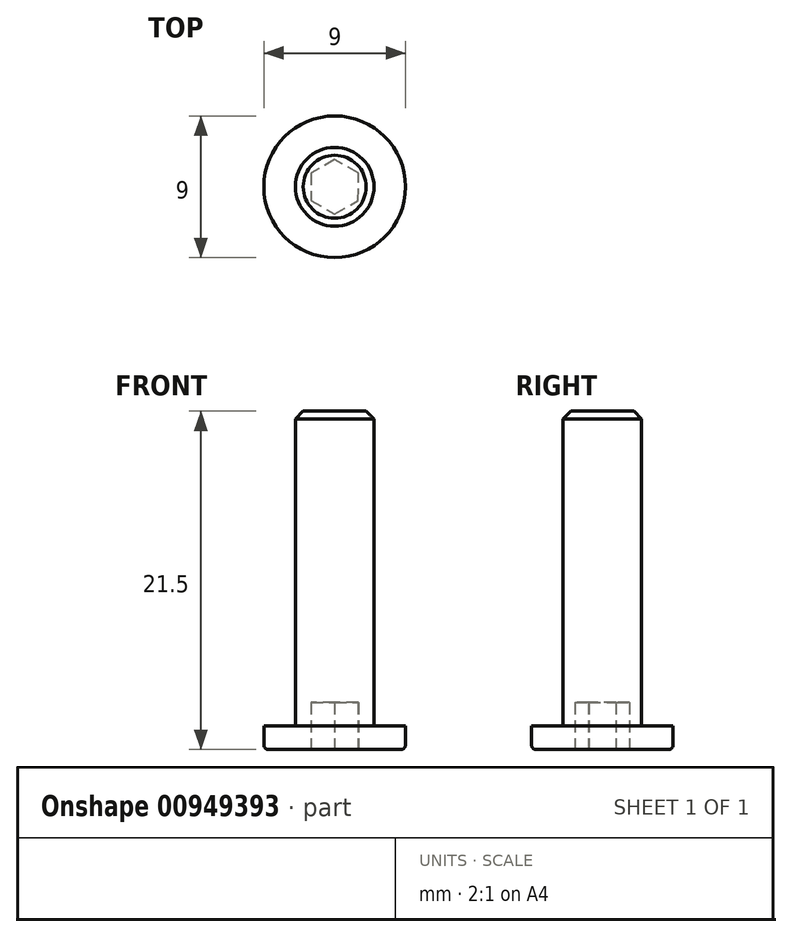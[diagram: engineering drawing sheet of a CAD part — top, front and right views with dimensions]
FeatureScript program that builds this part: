
annotation { "Feature Type Name" : "Feature", "Feature Type Description" : "" }
export const myFeature = defineFeature(function(context is Context, id is Id, definition is map)
    precondition{}
    {
        {
            var Q0;
            Q0=qCreatedBy(makeId("Top.planeOp"),FACE);
            var sketch = newSketch(context, id + "F0", { "sketchPlane" : qUnion([Q0])});
            skCircle(sketch, "E0", {"center": v(0, 0) * mm, "radius": 4.5 * mm});
            skCircle(sketch, "E1", {"center": v(0, 0) * mm, "radius": 2.5 * mm});
            skSolve(sketch);
        }
        {
            var Q0;
            Q0=makeQuery(id+"F0.imprint","IMPRINT",FACE,{"disambiguationData":[TD([[makeQuery(id+"F0.imprint","IMPRINT",EDGE,{"derivedFrom":sQuery(id+"F0.wireOp",EDGE,"E1")}),1.0]])]});
            extrude(context, id + "F1", {"entities" : qUnion([Q0]), "depth" : 20 * mm, "offsetDistance" : 25 * mm});
        }
        {
            var Q0;
            Q0 = qSketchRegion(id + "F0", true);
            var Q1;
            Q1=makeQuery(id+"F1.opExtrude","CAP_FACE",FACE,{"disambiguationData":[OSD([sQuery(id+"F0.wireOp",EDGE,"E1")])],"isStart":true});
            extrude(context, id + "F2", {"entities" : qUnion([Q0, Q1]), "operationType" : NewBodyOperationType.ADD, "oppositeDirection" : true, "depth" : 1.5 * mm, "offsetDistance" : 25 * mm});
        }
        {
            var Q0;
            {var subQ0=sQuery(id+"F0.wireOp",EDGE,"E1");Q0=makeQuery(id+"F2.boolean.opBoolean","MERGE",FACE,{"derivedFrom":[makeQuery(id+"F2.opExtrude","CAP_FACE",FACE,{"disambiguationData":[OSD([sQuery(id+"F0.wireOp",EDGE,"E0"),subQ0])],"isStart":false}),makeQuery(id+"F2.opExtrude","CAP_FACE",FACE,{"disambiguationData":[OSD([subQ0])],"isStart":false})]});}
            var sketch = newSketch(context, id + "F3", { "sketchPlane" : qUnion([Q0])});
            skCircle(sketch, "E2", {"center": v(0, 0) * mm, "radius": 3.75 * mm});
            skLineSegment(sketch, "E3.0", {"start": v(0, -1.73) * mm, "end": v(-1.5, -0.87) * mm});
            skLineSegment(sketch, "E3.1", {"start": v(-1.5, -0.87) * mm, "end": v(-1.5, 0.86) * mm});
            skLineSegment(sketch, "E3.2", {"start": v(-1.5, 0.86) * mm, "end": v(0, 1.73) * mm});
            skLineSegment(sketch, "E3.3", {"start": v(0, 1.73) * mm, "end": v(1.5, 0.87) * mm});
            skLineSegment(sketch, "E3.4", {"start": v(1.5, 0.87) * mm, "end": v(1.5, -0.86) * mm});
            skLineSegment(sketch, "E3.5", {"start": v(1.5, -0.86) * mm, "end": v(0, -1.73) * mm});
            skPoint(sketch, "E3.0.midPoint", {"position": v(-0.75, -1.3) * mm});
            skSolve(sketch);
        }
        {
            var Q0;
            Q0=makeQuery(id+"F2.opExtrude","CAP_EDGE",EDGE,{"disambiguationData":[OSD([sQuery(id+"F0.wireOp",EDGE,"E0")])],"isStart":false});
            fillet(context, id + "F4", {"entities" : qUnion([Q0]), "radius" : .3 * mm, "tangentPropagation" : true, "allowEdgeOverflow" : false});
        }
        {
            var Q0;
            Q0=makeQuery(id+"F3.imprint","IMPRINT",FACE,{"disambiguationData":[TD([[makeQuery(id+"F3.imprint","IMPRINT",EDGE,{"derivedFrom":sQuery(id+"F3.wireOp",EDGE,"E3.0")}),-1.0]])]});
            extrude(context, id + "F5", {"entities" : qUnion([Q0]), "operationType" : NewBodyOperationType.REMOVE, "oppositeDirection" : true, "depth" : 3 * mm, "offsetDistance" : 25 * mm});
        }
        {
            var Q0;
            Q0=makeQuery(id+"F1.opExtrude","CAP_EDGE",EDGE,{"disambiguationData":[OSD([sQuery(id+"F0.wireOp",EDGE,"E1")])],"isStart":false});
            chamfer(context, id + "F6", {"entities" : qUnion([Q0]), "width" : .5 * mm, "tangentPropagation" : true});
        }
    });
